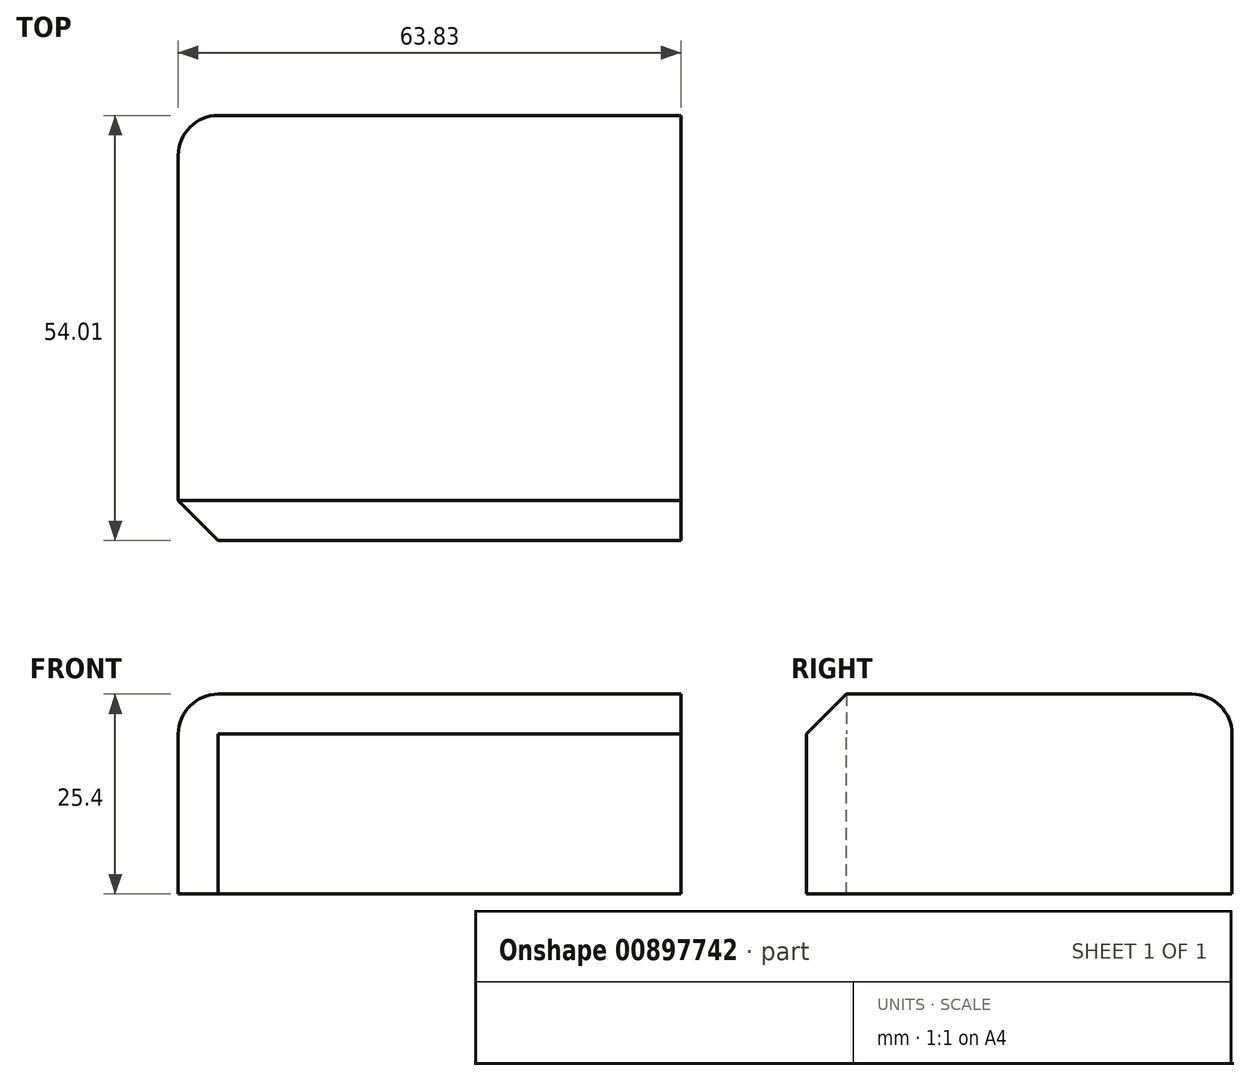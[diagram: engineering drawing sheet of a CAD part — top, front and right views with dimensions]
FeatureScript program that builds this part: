
annotation { "Feature Type Name" : "Feature", "Feature Type Description" : "" }
export const myFeature = defineFeature(function(context is Context, id is Id, definition is map)
    precondition{}
    {
        {
            var Q0;
            Q0=qCreatedBy(makeId("Top.planeOp"),FACE);
            var sketch = newSketch(context, id + "F0", { "sketchPlane" : qUnion([Q0])});
            skLineSegment(sketch, "E0.bottom", {"start": v(-33.58, 26.08) * mm, "end": v(30.25, 26.08) * mm});
            skLineSegment(sketch, "E0.top", {"start": v(-33.58, -27.93) * mm, "end": v(30.25, -27.93) * mm});
            skLineSegment(sketch, "E0.left", {"start": v(-33.58, 26.08) * mm, "end": v(-33.58, -27.93) * mm});
            skLineSegment(sketch, "E0.right", {"start": v(30.25, 26.08) * mm, "end": v(30.25, -27.93) * mm});
            skSolve(sketch);
        }
        {
            var Q0;
            Q0=makeQuery(id+"F0.imprint","IMPRINT",FACE,{"disambiguationData":[TD([[makeQuery(id+"F0.imprint","IMPRINT",EDGE,{"derivedFrom":sQuery(id+"F0.wireOp",EDGE,"E0.bottom")}),-1.0]])]});
            extrude(context, id + "F1", {"entities" : qUnion([Q0]), "oppositeDirection" : true, "depth" : 25.4 * mm, "offsetDistance" : 25.4 * mm});
        }
        {
            var Q0;
            Q0=makeQuery(id+"F1.opExtrude","CAP_EDGE",EDGE,{"disambiguationData":[OSD([sQuery(id+"F0.wireOp",EDGE,"E0.bottom")])],"isStart":true});
            fillet(context, id + "F2", {"entities" : qUnion([Q0]), "radius" : 5.08 * mm, "tangentPropagation" : true, "allowEdgeOverflow" : false});
        }
        {
            var Q0;
            Q0=makeQuery(id+"F1.opExtrude","CAP_EDGE",EDGE,{"disambiguationData":[OSD([sQuery(id+"F0.wireOp",EDGE,"E0.left")])],"isStart":true});
            fillet(context, id + "F3", {"entities" : qUnion([Q0]), "radius" : 5.08 * mm, "tangentPropagation" : true, "allowEdgeOverflow" : false});
        }
        {
            var Q0;
            Q0=makeQuery(id+"F1.opExtrude","CAP_EDGE",EDGE,{"disambiguationData":[OSD([sQuery(id+"F0.wireOp",EDGE,"E0.top")])],"isStart":true});
            chamfer(context, id + "F4", {"entities" : qUnion([Q0]), "width" : 5.08 * mm, "tangentPropagation" : true});
        }
    });
